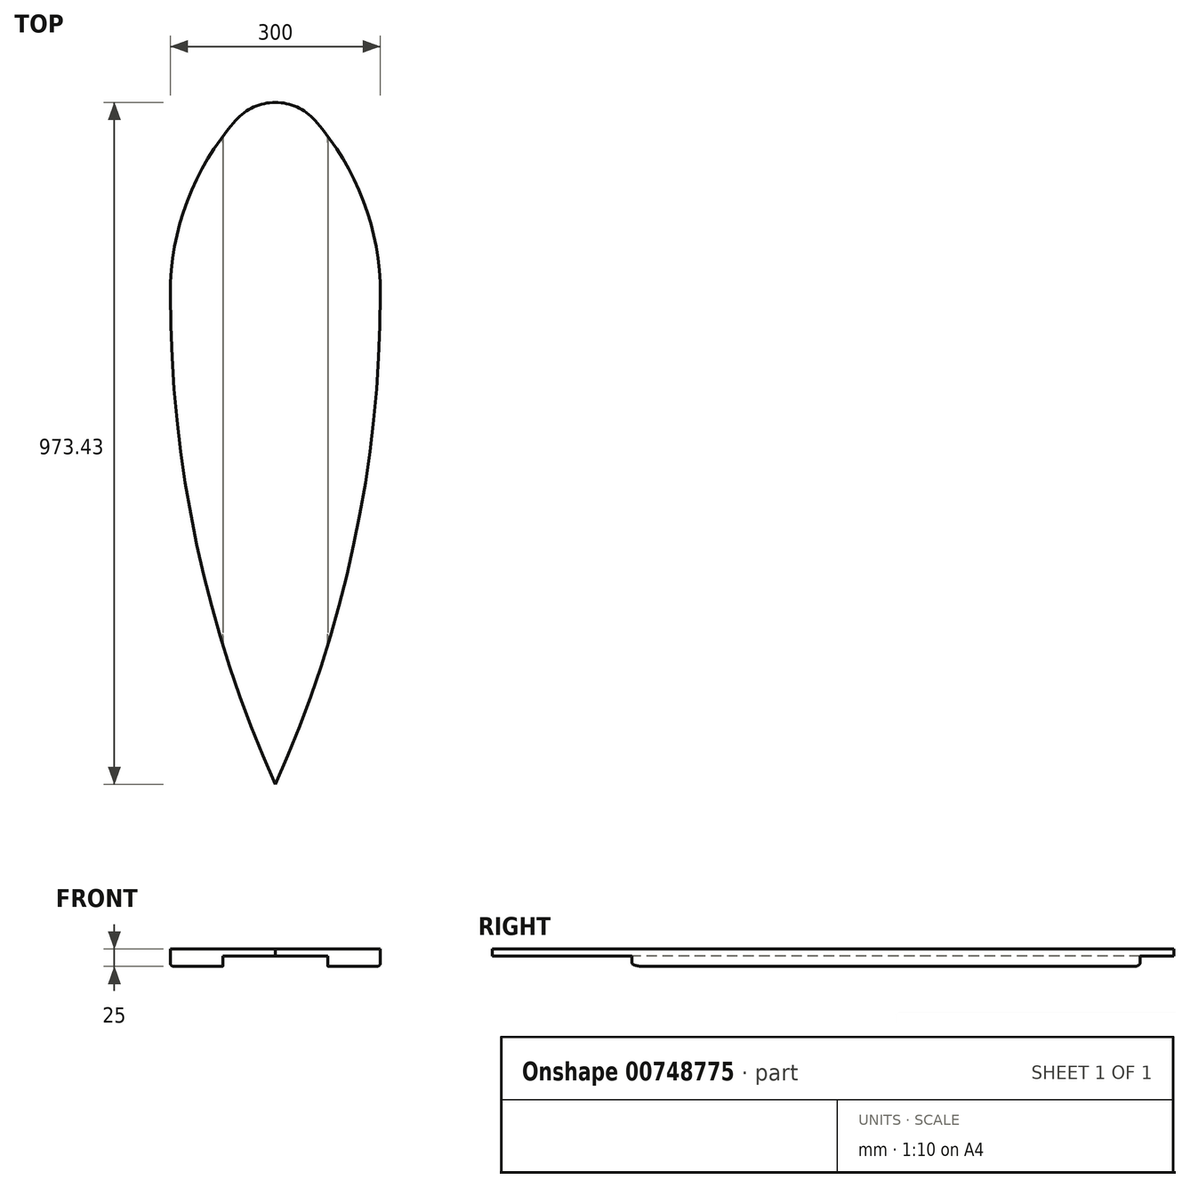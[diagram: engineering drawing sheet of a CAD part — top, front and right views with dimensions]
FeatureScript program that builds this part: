
annotation { "Feature Type Name" : "Feature", "Feature Type Description" : "" }
export const myFeature = defineFeature(function(context is Context, id is Id, definition is map)
    precondition{}
    {
        {
            var Q0;
            Q0=qCreatedBy(makeId("Top.planeOp"),FACE);
            var sketch = newSketch(context, id + "F0", { "sketchPlane" : qUnion([Q0])});
            skLineSegment(sketch, "E0.bottom", {"start": v(150, 500) * mm, "end": v(-150, 500) * mm, "construction": true});
            skLineSegment(sketch, "E0.top", {"start": v(150, -500) * mm, "end": v(-150, -500) * mm, "construction": true});
            skLineSegment(sketch, "E0.left", {"start": v(150, 500) * mm, "end": v(150, -500) * mm});
            skLineSegment(sketch, "E0.right", {"start": v(-150, 500) * mm, "end": v(-150, -500) * mm, "construction": true});
            skPoint(sketch, "E0.middle", {"position": v(0, 0) * mm});
            skLineSegment(sketch, "E1", {"start": v(0, 500) * mm, "end": v(0, -500) * mm, "construction": true});
            skPoint(sketch, "E2.orphan", {"position": v(0, 500) * mm});
            skArc(sketch, "E3", {"start": v(0, 500) * mm, "mid": v(-110.41, 367.7) * mm, "end": v(-150, 200) * mm});
            skArc(sketch, "E4.MirrorCS", {"start": v(150, 200) * mm, "mid": v(112.08, -157.95) * mm, "end": v(0, -500) * mm});
            skArc(sketch, "E5.MirrorCS", {"start": v(0, 500) * mm, "mid": v(110.41, 367.7) * mm, "end": v(150, 200) * mm});
            skArc(sketch, "E6.trimOffspring", {"start": v(-150, 200) * mm, "mid": v(-112.08, -157.95) * mm, "end": v(0, -500) * mm});
            skLineSegment(sketch, "E7", {"start": v(0, 200) * mm, "end": v(-1558.33, 200) * mm, "construction": true});
            skLineSegment(sketch, "E8", {"start": v(0, 200) * mm, "end": v(1558.33, 200) * mm, "construction": true});
            skSolve(sketch);
        }
        {
            var Q0;
            {var subQ3=sQuery(id+"F0.wireOp",EDGE,"E3");Q0=makeQuery(id+"F0.imprint","IMPRINT",FACE,{"disambiguationData":[TD([[makeQuery(id+"F0.imprint","IMPRINT",EDGE,{"derivedFrom":subQ3}),1.0]])]});}
            extrude(context, id + "F1", {"entities" : qUnion([Q0]), "depth" : 25 * mm, "offsetDistance" : 25 * mm});
        }
        {
            var Q0;
            Q0=makeQuery(id+"F1.opExtrude","SWEPT_EDGE",EDGE,{"disambiguationData":[OSD([sQuery(id+"F0.wireOp",EDGE,"E3"),sQuery(id+"F0.wireOp",EDGE,"E5.MirrorCS")])]});
            fillet(context, id + "F2", {"entities" : qUnion([Q0]), "radius" : 75 * mm, "tangentPropagation" : true, "allowEdgeOverflow" : false});
        }
        {
            var Q0;
            Q0=makeQuery(id+"F1.opExtrude","CAP_FACE",FACE,{"disambiguationData":[OSD([sQuery(id+"F0.wireOp",EDGE,"E3"),sQuery(id+"F0.wireOp",EDGE,"E4.MirrorCS"),sQuery(id+"F0.wireOp",EDGE,"E5.MirrorCS"),sQuery(id+"F0.wireOp",EDGE,"E6.trimOffspring")])],"isStart":true});
            fillet(context, id + "F3", {"entities" : qUnion([Q0]), "radius" : 5 * mm, "tangentPropagation" : true, "allowEdgeOverflow" : false});
        }
        {
            var Q0;
            Q0=qCreatedBy(makeId("Front.planeOp"),FACE);
            var sketch = newSketch(context, id + "F4", { "sketchPlane" : qUnion([Q0])});
            skLineSegment(sketch, "E9.bottom", {"start": v(-75, 15) * mm, "end": v(75, 15) * mm});
            skLineSegment(sketch, "E9.top", {"start": v(-75, -15) * mm, "end": v(75, -15) * mm});
            skLineSegment(sketch, "E9.left", {"start": v(-75, 15) * mm, "end": v(-75, -15) * mm});
            skLineSegment(sketch, "E9.right", {"start": v(75, 15) * mm, "end": v(75, -15) * mm});
            skPoint(sketch, "E9.middle", {"position": v(0, 0) * mm});
            skSolve(sketch);
        }
        {
            var Q0;
            Q0=makeQuery(id+"F4.imprint","IMPRINT",FACE,{"disambiguationData":[TD([[makeQuery(id+"F4.imprint","IMPRINT",EDGE,{"derivedFrom":sQuery(id+"F4.wireOp",EDGE,"E9.bottom")}),-1.0]])]});
            extrude(context, id + "F5", {"entities" : qUnion([Q0]), "operationType" : NewBodyOperationType.REMOVE, "endBound" : BoundingType.THROUGH_ALL, "oppositeDirection" : true, "depth" : 25 * mm, "offsetDistance" : 25 * mm, "hasSecondDirection" : true, "secondDirectionBound" : SecondDirectionBoundingType.THROUGH_ALL, "secondDirectionOppositeDirection" : false, "secondDirectionDepth" : 25 * mm});
        }
    });
